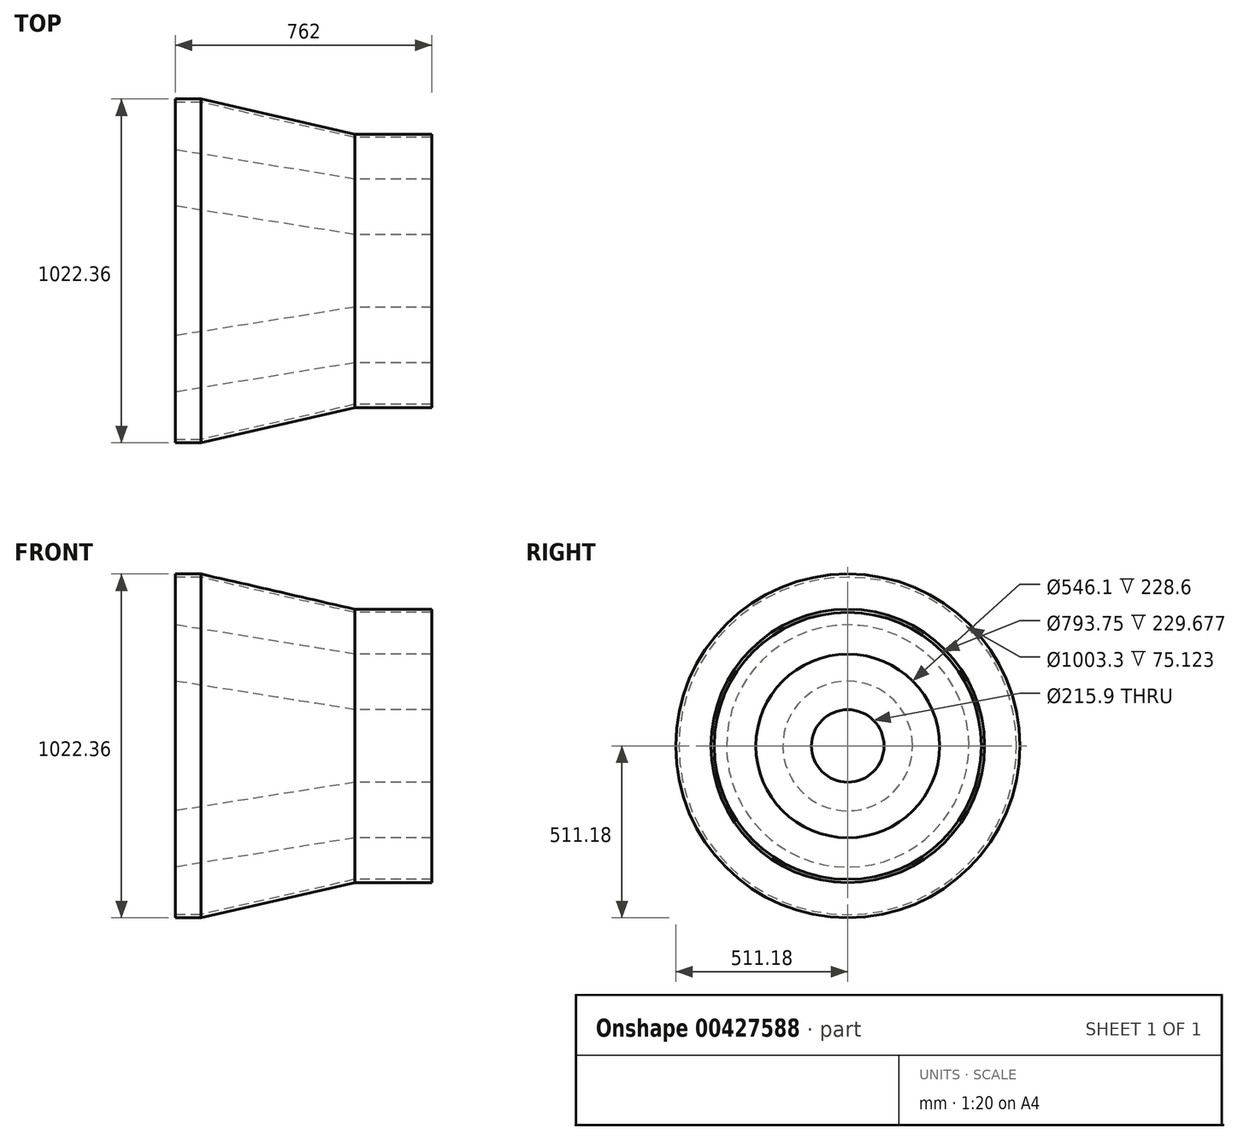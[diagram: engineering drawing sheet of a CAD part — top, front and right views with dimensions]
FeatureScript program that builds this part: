
annotation { "Feature Type Name" : "Feature", "Feature Type Description" : "" }
export const myFeature = defineFeature(function(context is Context, id is Id, definition is map)
    precondition{}
    {
        {
            var Q0;
            Q0=qCreatedBy(makeId("Front.planeOp"),FACE);
            var sketch = newSketch(context, id + "F0", { "sketchPlane" : qUnion([Q0])});
            skLineSegment(sketch, "E0", {"start": v(-381, 511.18) * mm, "end": v(-304.8, 511.18) * mm});
            skLineSegment(sketch, "E1", {"start": v(-304.8, 511.18) * mm, "end": v(152.4, 406.4) * mm});
            skLineSegment(sketch, "E2", {"start": v(152.4, 406.4) * mm, "end": v(381, 406.4) * mm});
            skLineSegment(sketch, "E3", {"start": v(-381, 0) * mm, "end": v(381, 0) * mm, "construction": true});
            skLineSegment(sketch, "E4", {"start": v(381, 0) * mm, "end": v(381, 721.34) * mm, "construction": true});
            skLineSegment(sketch, "E5.0", {"start": v(-381, 501.65) * mm, "end": v(-305.88, 501.65) * mm});
            skLineSegment(sketch, "E6.0", {"start": v(151.32, 396.87) * mm, "end": v(381, 396.87) * mm});
            skLineSegment(sketch, "E7.0", {"start": v(-305.88, 501.65) * mm, "end": v(151.32, 396.87) * mm});
            skLineSegment(sketch, "E8", {"start": v(152.4, 0) * mm, "end": v(152.4, 740.6) * mm, "construction": true});
            skLineSegment(sketch, "E9", {"start": v(-381, 0) * mm, "end": v(-381, 761.63) * mm, "construction": true});
            skLineSegment(sketch, "E10", {"start": v(-304.8, 0) * mm, "end": v(-304.8, 768.37) * mm, "construction": true});
            skLineSegment(sketch, "E11", {"start": v(381, 107.95) * mm, "end": v(152.4, 107.95) * mm});
            skLineSegment(sketch, "E12", {"start": v(152.4, 107.95) * mm, "end": v(-381, 192.88) * mm});
            skLineSegment(sketch, "E13", {"start": v(381, 273.05) * mm, "end": v(152.4, 273.05) * mm});
            skLineSegment(sketch, "E14", {"start": v(152.4, 273.05) * mm, "end": v(-381, 360.06) * mm});
            skLineSegment(sketch, "E15", {"start": v(381, 406.4) * mm, "end": v(381, 396.87) * mm});
            skLineSegment(sketch, "E16", {"start": v(-381, 511.18) * mm, "end": v(-381, 501.65) * mm});
            skLineSegment(sketch, "E17", {"start": v(-381, 501.65) * mm, "end": v(-381, 360.06) * mm});
            skLineSegment(sketch, "E18", {"start": v(381, 396.87) * mm, "end": v(381, 273.05) * mm});
            skLineSegment(sketch, "E19", {"start": v(-381, 360.06) * mm, "end": v(-381, 192.88) * mm});
            skLineSegment(sketch, "E20", {"start": v(381, 273.05) * mm, "end": v(381, 107.95) * mm});
            skSolve(sketch);
        }
        {
            var Q0;
            Q0=makeQuery(id+"F0.imprint","IMPRINT",FACE,{"disambiguationData":[TD([[makeQuery(id+"F0.imprint","IMPRINT",EDGE,{"derivedFrom":sQuery(id+"F0.wireOp",EDGE,"E11")}),-1.0]])]});
            var Q1;
            Q1=sQuery(id+"F0.wireOp",EDGE,"E3");
            revolve(context, id + "F1", {"entities" : qUnion([Q0]), "axis" : qUnion([Q1]), "revolveType" : RevolveType.FULL});
        }
        {
            var Q0;
            Q0=makeQuery(id+"F0.imprint","IMPRINT",FACE,{"disambiguationData":[TD([[makeQuery(id+"F0.imprint","IMPRINT",EDGE,{"derivedFrom":sQuery(id+"F0.wireOp",EDGE,"E5.0")}),-1.0]])]});
            var Q1;
            Q1=sQuery(id+"F0.wireOp",EDGE,"E3");
            revolve(context, id + "F2", {"entities" : qUnion([Q0]), "axis" : qUnion([Q1]), "revolveType" : RevolveType.FULL});
        }
        {
            var Q0;
            Q0=makeQuery(id+"F0.imprint","IMPRINT",FACE,{"disambiguationData":[TD([[makeQuery(id+"F0.imprint","IMPRINT",EDGE,{"derivedFrom":sQuery(id+"F0.wireOp",EDGE,"E0")}),-1.0]])]});
            var Q1;
            Q1=sQuery(id+"F0.wireOp",EDGE,"E3");
            revolve(context, id + "F3", {"entities" : qUnion([Q0]), "axis" : qUnion([Q1]), "revolveType" : RevolveType.FULL});
        }
    });
